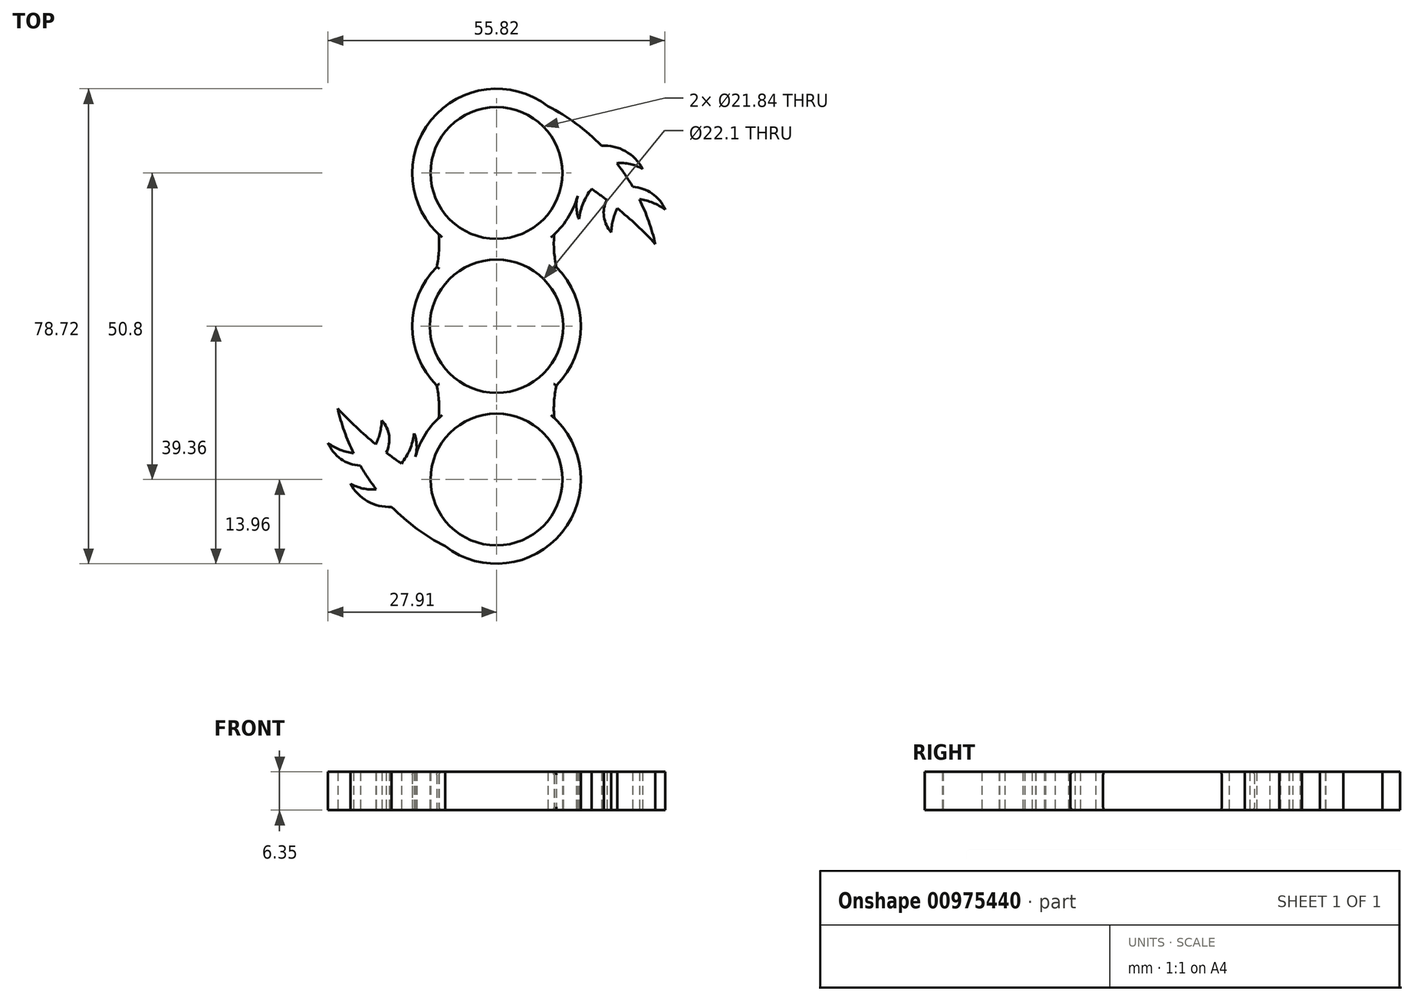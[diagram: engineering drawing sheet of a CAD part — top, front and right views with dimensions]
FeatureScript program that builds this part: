
annotation { "Feature Type Name" : "Feature", "Feature Type Description" : "" }
export const myFeature = defineFeature(function(context is Context, id is Id, definition is map)
    precondition{}
    {
        {
            var Q0;
            Q0=qCreatedBy(makeId("Top.planeOp"),FACE);
            var sketch = newSketch(context, id + "F0", { "sketchPlane" : qUnion([Q0])});
            skCircle(sketch, "E0", {"center": v(0, 0) * mm, "radius": 13.97 * mm});
            skArc(sketch, "E1", {"start": v(9.57, 15.23) * mm, "mid": v(9.53, 12.51) * mm, "end": v(9.93, 9.82) * mm});
            skArc(sketch, "E2.MirrorCS", {"start": v(-9.57, 15.23) * mm, "mid": v(-9.53, 12.51) * mm, "end": v(-9.93, 9.82) * mm});
            skArc(sketch, "E3.MirrorCS", {"start": v(9.57, -15.23) * mm, "mid": v(9.53, -12.51) * mm, "end": v(9.93, -9.82) * mm});
            skArc(sketch, "E4.MirrorCS", {"start": v(-9.57, -15.23) * mm, "mid": v(-9.53, -12.51) * mm, "end": v(-9.93, -9.82) * mm});
            skCircle(sketch, "E5", {"center": v(0, 0) * mm, "radius": 11.05 * mm});
            skCircle(sketch, "E6", {"center": v(0, 25.4) * mm, "radius": 10.92 * mm});
            skCircle(sketch, "E7.MirrorC", {"center": v(0, -25.4) * mm, "radius": 10.92 * mm});
            skArc(sketch, "E8", {"start": v(9.57, 15.23) * mm, "mid": v(0, 39.36) * mm, "end": v(-9.57, 15.23) * mm});
            skArc(sketch, "E9", {"start": v(-9.57, -15.23) * mm, "mid": v(0, -39.36) * mm, "end": v(9.57, -15.23) * mm});
            skArc(sketch, "E10", {"start": v(26.31, 13.62) * mm, "mid": v(19.93, 27) * mm, "end": v(8.51, 36.46) * mm});
            skArc(sketch, "E11", {"start": v(26.31, 13.62) * mm, "mid": v(20.44, 19.2) * mm, "end": v(13.9, 24) * mm});
            skArc(sketch, "E12", {"start": v(24.21, 26.08) * mm, "mid": v(21.36, 29.01) * mm, "end": v(17.38, 29.93) * mm});
            skArc(sketch, "E13", {"start": v(24.21, 26.08) * mm, "mid": v(22.15, 26.88) * mm, "end": v(19.93, 27) * mm});
            skPoint(sketch, "E13.midSnap0", {"position": v(19.93, 27) * mm});
            skPoint(sketch, "E13.midSnap1", {"position": v(21.36, 29.01) * mm});
            skArc(sketch, "E14", {"start": v(27.91, 19.35) * mm, "mid": v(25.78, 22) * mm, "end": v(22.57, 23.1) * mm});
            skArc(sketch, "E15", {"start": v(27.91, 19.35) * mm, "mid": v(25.9, 20.47) * mm, "end": v(23.67, 21.04) * mm});
            skArc(sketch, "E16", {"start": v(18.27, 20.94) * mm, "mid": v(17.8, 18.15) * mm, "end": v(19, 15.6) * mm});
            skArc(sketch, "E17", {"start": v(20, 19.57) * mm, "mid": v(19.3, 17.63) * mm, "end": v(19, 15.6) * mm});
            skArc(sketch, "E18", {"start": v(13.44, 21.62) * mm, "mid": v(13.24, 19.68) * mm, "end": v(13.64, 17.77) * mm});
            skArc(sketch, "E19", {"start": v(15.74, 22.77) * mm, "mid": v(14.36, 20.4) * mm, "end": v(13.64, 17.77) * mm});
            skArc(sketch, "E20.MirrorCS", {"start": v(-26.31, -13.62) * mm, "mid": v(-20.44, -19.2) * mm, "end": v(-13.9, -24) * mm});
            skArc(sketch, "E21.MirrorCS", {"start": v(-27.91, -19.35) * mm, "mid": v(-25.9, -20.47) * mm, "end": v(-23.67, -21.04) * mm});
            skArc(sketch, "E22.MirrorCS", {"start": v(-24.21, -26.08) * mm, "mid": v(-22.15, -26.88) * mm, "end": v(-19.93, -27) * mm});
            skArc(sketch, "E23.MirrorCS", {"start": v(-15.74, -22.77) * mm, "mid": v(-14.36, -20.4) * mm, "end": v(-13.64, -17.77) * mm});
            skArc(sketch, "E24.MirrorCS", {"start": v(-24.21, -26.08) * mm, "mid": v(-21.36, -29.01) * mm, "end": v(-17.38, -29.93) * mm});
            skArc(sketch, "E25.MirrorCS", {"start": v(-27.91, -19.35) * mm, "mid": v(-25.78, -22) * mm, "end": v(-22.57, -23.1) * mm});
            skArc(sketch, "E26.MirrorCS", {"start": v(-18.27, -20.94) * mm, "mid": v(-17.8, -18.15) * mm, "end": v(-19, -15.6) * mm});
            skArc(sketch, "E27.MirrorCS", {"start": v(-20, -19.57) * mm, "mid": v(-19.3, -17.63) * mm, "end": v(-19, -15.6) * mm});
            skPoint(sketch, "E28.MirrorP", {"position": v(-19.93, -27) * mm});
            skPoint(sketch, "E29.MirrorP", {"position": v(-21.36, -29.01) * mm});
            skArc(sketch, "E30.MirrorCS", {"start": v(-26.31, -13.62) * mm, "mid": v(-19.93, -27) * mm, "end": v(-8.51, -36.46) * mm});
            skArc(sketch, "E31.MirrorCS", {"start": v(-13.44, -21.62) * mm, "mid": v(-13.24, -19.68) * mm, "end": v(-13.64, -17.77) * mm});
            skSolve(sketch);
        }
        {
            var Q0;
            {var subQ0=sQuery(id+"F0.wireOp",EDGE,"e6c8af6f-f025-454f-92b2-53991b79567a0.MirrorC");var subQ1=makeQuery(id+"F0.imprint","INTERSECT",VERTEX,{"derivedFrom":[subQ0,sQuery(id+"F0.wireOp",EDGE,"E3.MirrorCS")]});Q0=makeQuery(id+"F0.imprint","IMPRINT",FACE,{"disambiguationData":[TD([[makeQuery(id+"F0.imprint","IMPRINT",EDGE,{"disambiguationData":[TD([[subQ1,1.0]])],"derivedFrom":subQ0}),-1.0]])]});}
            var Q1;
            {var subQ0=sQuery(id+"F0.wireOp",EDGE,"E3.MirrorCS");Q1=makeQuery(id+"F0.imprint","IMPRINT",FACE,{"disambiguationData":[TD([[makeQuery(id+"F0.imprint","IMPRINT",EDGE,{"derivedFrom":subQ0}),1.0]])]});}
            var Q2;
            {var subQ0=sQuery(id+"F0.wireOp",EDGE,"e6c8af6f-f025-454f-92b2-53991b79567a0.MirrorC");var subQ1=makeQuery(id+"F0.imprint","INTERSECT",VERTEX,{"derivedFrom":[subQ0,sQuery(id+"F0.wireOp",EDGE,"E3.MirrorCS")]});Q2=makeQuery(id+"F0.imprint","IMPRINT",FACE,{"disambiguationData":[TD([[makeQuery(id+"F0.imprint","IMPRINT",EDGE,{"disambiguationData":[TD([[subQ1,1.0]])],"derivedFrom":subQ0}),-1.0]])]});}
            var Q3;
            {var subQ0=sQuery(id+"F0.wireOp",EDGE,"E1");Q3=makeQuery(id+"F0.imprint","IMPRINT",FACE,{"disambiguationData":[TD([[makeQuery(id+"F0.imprint","IMPRINT",EDGE,{"derivedFrom":subQ0}),-1.0]])]});}
            var Q4;
            {var subQ0=sQuery(id+"F0.wireOp",EDGE,"9b569017-5ae3-447a-a9db-ab0b89fc7daf");var subQ1=makeQuery(id+"F0.imprint","INTERSECT",VERTEX,{"derivedFrom":[subQ0,sQuery(id+"F0.wireOp",EDGE,"E1")]});Q4=makeQuery(id+"F0.imprint","IMPRINT",FACE,{"disambiguationData":[TD([[makeQuery(id+"F0.imprint","IMPRINT",EDGE,{"disambiguationData":[TD([[subQ1,1.0]])],"derivedFrom":subQ0}),1.0]])]});}
            var Q5;
            {var subQ0=sQuery(id+"F0.wireOp",EDGE,"E3.MirrorCS");Q5=makeQuery(id+"F0.imprint","IMPRINT",FACE,{"disambiguationData":[TD([[makeQuery(id+"F0.imprint","IMPRINT",EDGE,{"derivedFrom":subQ0}),1.0]])]});}
            var Q6;
            {var subQ0=sQuery(id+"F0.wireOp",EDGE,"E0");var subQ1=makeQuery(id+"F0.imprint","INTERSECT",VERTEX,{"derivedFrom":[subQ0,sQuery(id+"F0.wireOp",EDGE,"E1")]});Q6=makeQuery(id+"F0.imprint","IMPRINT",FACE,{"disambiguationData":[TD([[makeQuery(id+"F0.imprint","IMPRINT",EDGE,{"disambiguationData":[TD([[subQ1,-1.0]])],"derivedFrom":subQ0}),1.0]])]});}
            var Q7;
            {var subQ0=sQuery(id+"F0.wireOp",EDGE,"E2.MirrorCS");Q7=makeQuery(id+"F0.imprint","IMPRINT",FACE,{"disambiguationData":[TD([[makeQuery(id+"F0.imprint","IMPRINT",EDGE,{"derivedFrom":subQ0}),1.0]])]});}
            var Q8;
            {var subQ0=sQuery(id+"F0.wireOp",EDGE,"E4.MirrorCS");Q8=makeQuery(id+"F0.imprint","IMPRINT",FACE,{"disambiguationData":[TD([[makeQuery(id+"F0.imprint","IMPRINT",EDGE,{"derivedFrom":subQ0}),-1.0]])]});}
            var Q9;
            {var subQ3=sQuery(id+"F0.wireOp",EDGE,"E11");Q9=makeQuery(id+"F0.imprint","IMPRINT",FACE,{"disambiguationData":[TD([[makeQuery(id+"F0.imprint","IMPRINT",EDGE,{"derivedFrom":subQ3}),-1.0]])]});}
            var Q10;
            {var subQ0=sQuery(id+"F0.wireOp",EDGE,"E12");Q10=makeQuery(id+"F0.imprint","IMPRINT",FACE,{"disambiguationData":[TD([[makeQuery(id+"F0.imprint","IMPRINT",EDGE,{"derivedFrom":subQ0}),1.0]])]});}
            var Q11;
            {var subQ0=sQuery(id+"F0.wireOp",EDGE,"E14");Q11=makeQuery(id+"F0.imprint","IMPRINT",FACE,{"disambiguationData":[TD([[makeQuery(id+"F0.imprint","IMPRINT",EDGE,{"derivedFrom":subQ0}),1.0]])]});}
            var Q12;
            {var subQ0=sQuery(id+"F0.wireOp",EDGE,"E20.MirrorCS");var subQ9=sQuery(id+"F0.wireOp",EDGE,"E9");var subQ10=makeQuery(id+"F0.imprint","INTERSECT",VERTEX,{"derivedFrom":[subQ9,subQ0]});Q12=makeQuery(id+"F0.imprint","IMPRINT",FACE,{"disambiguationData":[TD([[makeQuery(id+"F0.imprint","IMPRINT",EDGE,{"disambiguationData":[TD([[subQ10,-1.0]])],"derivedFrom":subQ9}),-1.0]])]});}
            var Q13;
            {var subQ4=sQuery(id+"F0.wireOp",EDGE,"E23.MirrorCS");Q13=makeQuery(id+"F0.imprint","IMPRINT",FACE,{"disambiguationData":[TD([[makeQuery(id+"F0.imprint","IMPRINT",EDGE,{"derivedFrom":subQ4}),-1.0]])]});}
            var Q14;
            {var subQ0=sQuery(id+"F0.wireOp",EDGE,"E26.MirrorCS");Q14=makeQuery(id+"F0.imprint","IMPRINT",FACE,{"disambiguationData":[TD([[makeQuery(id+"F0.imprint","IMPRINT",EDGE,{"derivedFrom":subQ0}),1.0]])]});}
            var Q15;
            {var subQ0=sQuery(id+"F0.wireOp",EDGE,"E21.MirrorCS");Q15=makeQuery(id+"F0.imprint","IMPRINT",FACE,{"disambiguationData":[TD([[makeQuery(id+"F0.imprint","IMPRINT",EDGE,{"derivedFrom":subQ0}),-1.0]])]});}
            var Q16;
            {var subQ0=sQuery(id+"F0.wireOp",EDGE,"E22.MirrorCS");Q16=makeQuery(id+"F0.imprint","IMPRINT",FACE,{"disambiguationData":[TD([[makeQuery(id+"F0.imprint","IMPRINT",EDGE,{"derivedFrom":subQ0}),-1.0]])]});}
            var Q17;
            {var subQ0=sQuery(id+"F0.wireOp",EDGE,"E16");Q17=makeQuery(id+"F0.imprint","IMPRINT",FACE,{"disambiguationData":[TD([[makeQuery(id+"F0.imprint","IMPRINT",EDGE,{"derivedFrom":subQ0}),1.0]])]});}
            var Q18;
            {var subQ3=sQuery(id+"F0.wireOp",EDGE,"E18");Q18=makeQuery(id+"F0.imprint","IMPRINT",FACE,{"disambiguationData":[TD([[makeQuery(id+"F0.imprint","IMPRINT",EDGE,{"derivedFrom":subQ3}),1.0]])]});}
            extrude(context, id + "F1", {"entities" : qUnion([Q0, Q1, Q2, Q3, Q4, Q5, Q6, Q7, Q8, Q9, Q10, Q11, Q12, Q13, Q14, Q15, Q16, Q17, Q18]), "depth" : 6.35 * mm, "offsetDistance" : 25.4 * mm});
        }
        {
            var Q0;
            {var subQ0=sQuery(id+"F0.wireOp",EDGE,"E0");Q0=makeQuery(id+"F1.opExtrude","CAP_EDGE",EDGE,{"disambiguationData":[OSD([subQ0]),TDD([makeQuery(id+"F0.imprint","IMPRINT",EDGE,{"disambiguationData":[TD([[makeQuery(id+"F0.imprint","INTERSECT",VERTEX,{"derivedFrom":[subQ0,sQuery(id+"F0.wireOp",EDGE,"E1")]}),1.0]])],"derivedFrom":subQ0})])],"isStart":false});}
            var Q1;
            {var subQ0=sQuery(id+"F0.wireOp",EDGE,"E0");Q1=makeQuery(id+"F1.opExtrude","CAP_EDGE",EDGE,{"disambiguationData":[OSD([subQ0]),TDD([makeQuery(id+"F0.imprint","IMPRINT",EDGE,{"disambiguationData":[TD([[makeQuery(id+"F0.imprint","INTERSECT",VERTEX,{"derivedFrom":[subQ0,sQuery(id+"F0.wireOp",EDGE,"E2.MirrorCS")]}),-1.0]])],"derivedFrom":subQ0})])],"isStart":false});}
            var Q2;
            Q2=makeQuery(id+"F1.opExtrude","CAP_EDGE",EDGE,{"disambiguationData":[OSD([sQuery(id+"F0.wireOp",EDGE,"E1")])],"isStart":false});
            var Q3;
            Q3=makeQuery(id+"F1.opExtrude","CAP_EDGE",EDGE,{"disambiguationData":[OSD([sQuery(id+"F0.wireOp",EDGE,"E3.MirrorCS")])],"isStart":false});
            var Q4;
            Q4=makeQuery(id+"F1.opExtrude","CAP_EDGE",EDGE,{"disambiguationData":[OSD([sQuery(id+"F0.wireOp",EDGE,"E4.MirrorCS")])],"isStart":false});
            var Q5;
            Q5=makeQuery(id+"F1.opExtrude","CAP_EDGE",EDGE,{"disambiguationData":[OSD([sQuery(id+"F0.wireOp",EDGE,"E2.MirrorCS")])],"isStart":false});
            var Q6;
            {var subQ0=sQuery(id+"F0.wireOp",EDGE,"E0");Q6=makeQuery(id+"F1.opExtrude","CAP_EDGE",EDGE,{"disambiguationData":[OSD([subQ0]),TDD([makeQuery(id+"F0.imprint","IMPRINT",EDGE,{"disambiguationData":[TD([[makeQuery(id+"F0.imprint","INTERSECT",VERTEX,{"derivedFrom":[subQ0,sQuery(id+"F0.wireOp",EDGE,"E2.MirrorCS")]}),-1.0]])],"derivedFrom":subQ0})])],"isStart":true});}
            var Q7;
            Q7=makeQuery(id+"F1.opExtrude","CAP_EDGE",EDGE,{"disambiguationData":[OSD([sQuery(id+"F0.wireOp",EDGE,"E2.MirrorCS")])],"isStart":true});
            var Q8;
            Q8=makeQuery(id+"F1.opExtrude","CAP_EDGE",EDGE,{"disambiguationData":[OSD([sQuery(id+"F0.wireOp",EDGE,"E1")])],"isStart":true});
            var Q9;
            {var subQ0=sQuery(id+"F0.wireOp",EDGE,"E0");Q9=makeQuery(id+"F1.opExtrude","CAP_EDGE",EDGE,{"disambiguationData":[OSD([subQ0]),TDD([makeQuery(id+"F0.imprint","IMPRINT",EDGE,{"disambiguationData":[TD([[makeQuery(id+"F0.imprint","INTERSECT",VERTEX,{"derivedFrom":[subQ0,sQuery(id+"F0.wireOp",EDGE,"E1")]}),1.0]])],"derivedFrom":subQ0})])],"isStart":true});}
            var Q10;
            Q10=makeQuery(id+"F1.opExtrude","CAP_EDGE",EDGE,{"disambiguationData":[OSD([sQuery(id+"F0.wireOp",EDGE,"E3.MirrorCS")])],"isStart":true});
            var Q11;
            Q11=makeQuery(id+"F1.opExtrude","CAP_EDGE",EDGE,{"disambiguationData":[OSD([sQuery(id+"F0.wireOp",EDGE,"E4.MirrorCS")])],"isStart":true});
            fillet(context, id + "F2", {"entities" : qUnion([Q0, Q1, Q2, Q3, Q4, Q5, Q6, Q7, Q8, Q9, Q10, Q11]), "radius" : 0.5 * mm, "tangentPropagation" : true, "allowEdgeOverflow" : false});
        }
    });
